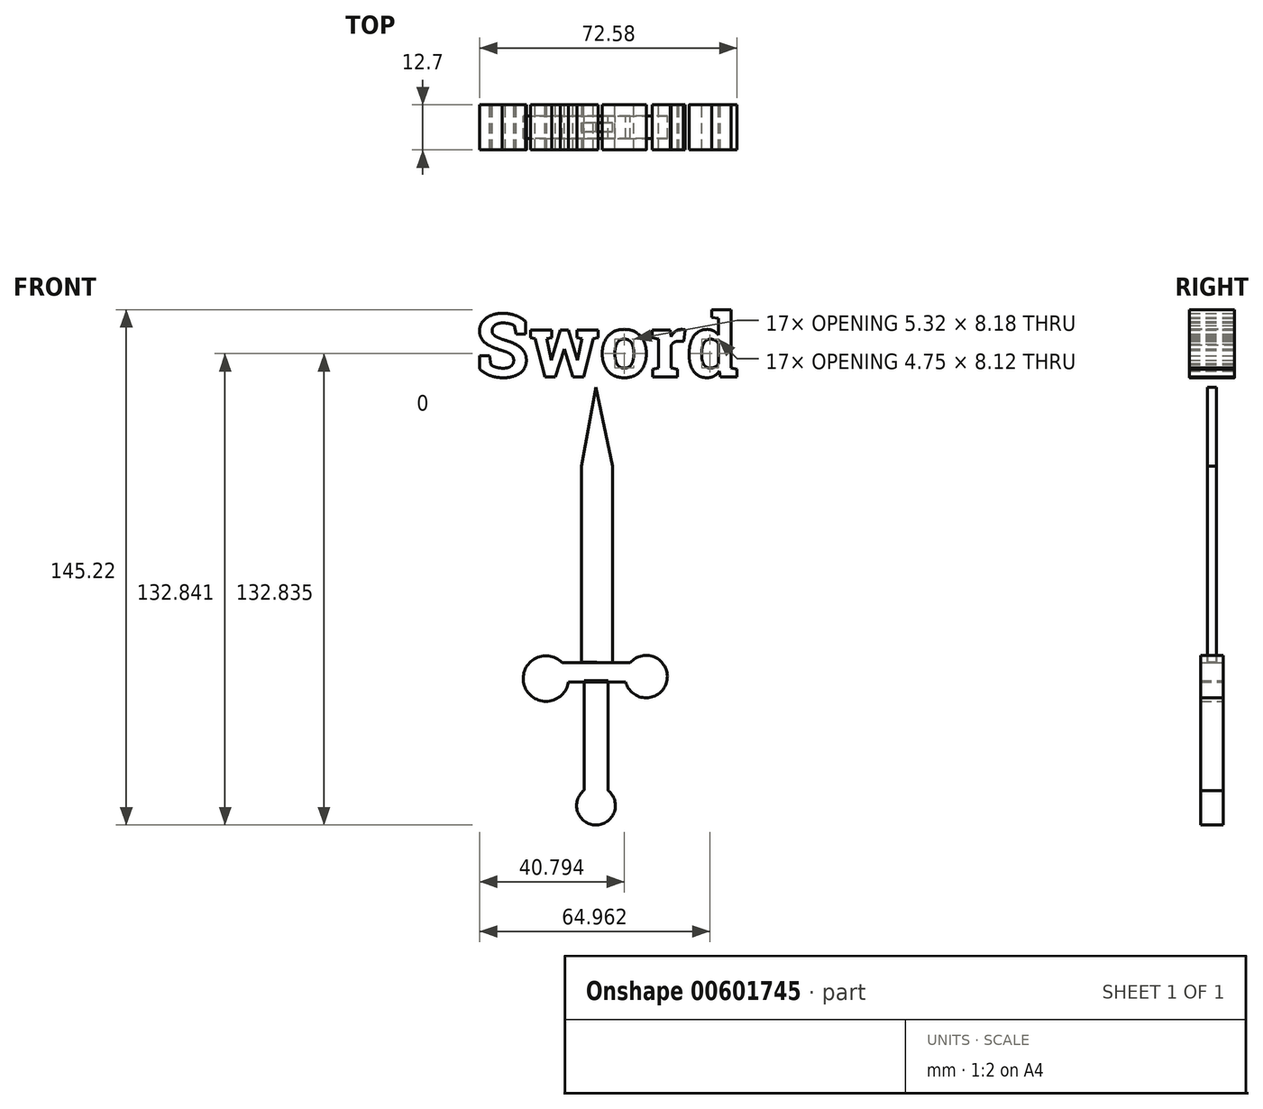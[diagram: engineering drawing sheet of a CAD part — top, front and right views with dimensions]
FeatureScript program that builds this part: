
annotation { "Feature Type Name" : "Feature", "Feature Type Description" : "" }
export const myFeature = defineFeature(function(context is Context, id is Id, definition is map)
    precondition{}
    {
        {
            var Q0;
            Q0=qCreatedBy(makeId("Front.planeOp"),FACE);
            var sketch = newSketch(context, id + "F0", { "sketchPlane" : qUnion([Q0])});
            skLineSegment(sketch, "E0.bottom", {"start": v(-3.32, -31.7) * mm, "end": v(3.43, -31.7) * mm});
            skLineSegment(sketch, "E0.top", {"start": v(-3.32, -63.46) * mm, "end": v(3.43, -63.46) * mm});
            skLineSegment(sketch, "E0.left", {"start": v(-3.32, -31.7) * mm, "end": v(-3.32, -63.46) * mm});
            skLineSegment(sketch, "E0.right", {"start": v(3.43, -31.7) * mm, "end": v(3.43, -63.46) * mm});
            skSolve(sketch);
        }
        {
            var Q0;
            Q0 = qSketchRegion(id + "F0", true);
            extrude(context, id + "F1", {"entities" : qUnion([Q0]), "endBound" : BoundingType.SYMMETRIC, "depth" : 6.35 * mm, "offsetDistance" : 25.4 * mm});
        }
        {
            var Q0;
            Q0=qCreatedBy(makeId("Front.planeOp"),FACE);
            var sketch = newSketch(context, id + "F2", { "sketchPlane" : qUnion([Q0])});
            skLineSegment(sketch, "E1", {"start": v(0, -32.11) * mm, "end": v(9.55, -32.11) * mm});
            skLineSegment(sketch, "E2", {"start": v(9.55, -32.11) * mm, "end": v(17.21, -26.7) * mm});
            skLineSegment(sketch, "E3", {"start": v(17.21, -26.7) * mm, "end": v(-16.84, -26.7) * mm});
            skLineSegment(sketch, "E4", {"start": v(-16.84, -26.7) * mm, "end": v(-8.46, -32.11) * mm});
            skLineSegment(sketch, "E5", {"start": v(-8.46, -32.11) * mm, "end": v(0, -32.11) * mm});
            skSolve(sketch);
        }
        {
            var Q0;
            Q0 = qSketchRegion(id + "F2", true);
            extrude(context, id + "F3", {"entities" : qUnion([Q0]), "endBound" : BoundingType.SYMMETRIC, "depth" : 6.35 * mm, "offsetDistance" : 25.4 * mm});
        }
        {
            var Q0;
            Q0=qCreatedBy(makeId("Front.planeOp"),FACE);
            var sketch = newSketch(context, id + "F4", { "sketchPlane" : qUnion([Q0])});
            skCircle(sketch, "E6", {"center": v(0, -66.97) * mm, "radius": 5.46 * mm});
            skSolve(sketch);
        }
        {
            var Q0;
            Q0 = qSketchRegion(id + "F4", true);
            extrude(context, id + "F5", {"entities" : qUnion([Q0]), "operationType" : NewBodyOperationType.ADD, "endBound" : BoundingType.SYMMETRIC, "depth" : 6.35 * mm, "offsetDistance" : 25.4 * mm});
        }
        {
            var Q0;
            Q0=qCreatedBy(makeId("Front.planeOp"),FACE);
            var sketch = newSketch(context, id + "F6", { "sketchPlane" : qUnion([Q0])});
            skLineSegment(sketch, "E7", {"start": v(-4.06, -26.46) * mm, "end": v(-4.06, 28.67) * mm});
            skLineSegment(sketch, "E8", {"start": v(-4.06, 28.67) * mm, "end": v(0, 50.87) * mm});
            skLineSegment(sketch, "E9", {"start": v(0, 50.87) * mm, "end": v(4.62, 28.67) * mm});
            skLineSegment(sketch, "E10", {"start": v(4.62, 28.67) * mm, "end": v(4.62, -26.7) * mm});
            skLineSegment(sketch, "E11", {"start": v(4.62, -26.7) * mm, "end": v(-4.06, -26.46) * mm});
            skSolve(sketch);
        }
        {
            var Q0;
            Q0 = qSketchRegion(id + "F6", true);
            extrude(context, id + "F7", {"entities" : qUnion([Q0]), "endBound" : BoundingType.SYMMETRIC, "depth" : 2.54 * mm, "offsetDistance" : 25.4 * mm});
        }
        {
            var Q0;
            Q0=qCreatedBy(makeId("Front.planeOp"),FACE);
            var sketch = newSketch(context, id + "F8", { "sketchPlane" : qUnion([Q0])});
            skCircle(sketch, "E12", {"center": v(14.13, -30.63) * mm, "radius": 5.97 * mm});
            skSolve(sketch);
        }
        {
            var Q0;
            Q0 = qSketchRegion(id + "F8", true);
            extrude(context, id + "F9", {"entities" : qUnion([Q0]), "operationType" : NewBodyOperationType.ADD, "endBound" : BoundingType.SYMMETRIC, "depth" : 6.35 * mm, "offsetDistance" : 25.4 * mm});
        }
        {
            var Q0;
            Q0=qCreatedBy(makeId("Front.planeOp"),FACE);
            var sketch = newSketch(context, id + "F10", { "sketchPlane" : qUnion([Q0])});
            skCircle(sketch, "E13", {"center": v(-14.13, -31.2) * mm, "radius": 6.4 * mm});
            skSolve(sketch);
        }
        {
            var Q0;
            Q0 = qSketchRegion(id + "F10", true);
            extrude(context, id + "F11", {"entities" : qUnion([Q0]), "operationType" : NewBodyOperationType.ADD, "endBound" : BoundingType.SYMMETRIC, "depth" : 6.35 * mm, "offsetDistance" : 25.4 * mm});
        }
        {
            var Q0;
            Q0=qCreatedBy(makeId("Front.planeOp"),FACE);
            var sketch = newSketch(context, id + "F12", { "sketchPlane" : qUnion([Q0])});
            skText(sketch, "E14", { "text": "Sword", "fontName": "RobotoSlab-Bold.ttf"});
            const initialGuessF12  = {"E14": [-0.034, 0.05385, 1, 0, 0.0179]};
            skSetInitialGuess(sketch, initialGuessF12);
            skSolve(sketch);
        }
        {
            var Q0;
            Q0 = qSketchRegion(id + "F12", true);
            extrude(context, id + "F13", {"entities" : qUnion([Q0]), "endBound" : BoundingType.SYMMETRIC, "depth" : 12.7 * mm, "offsetDistance" : 25.4 * mm});
        }
    });
